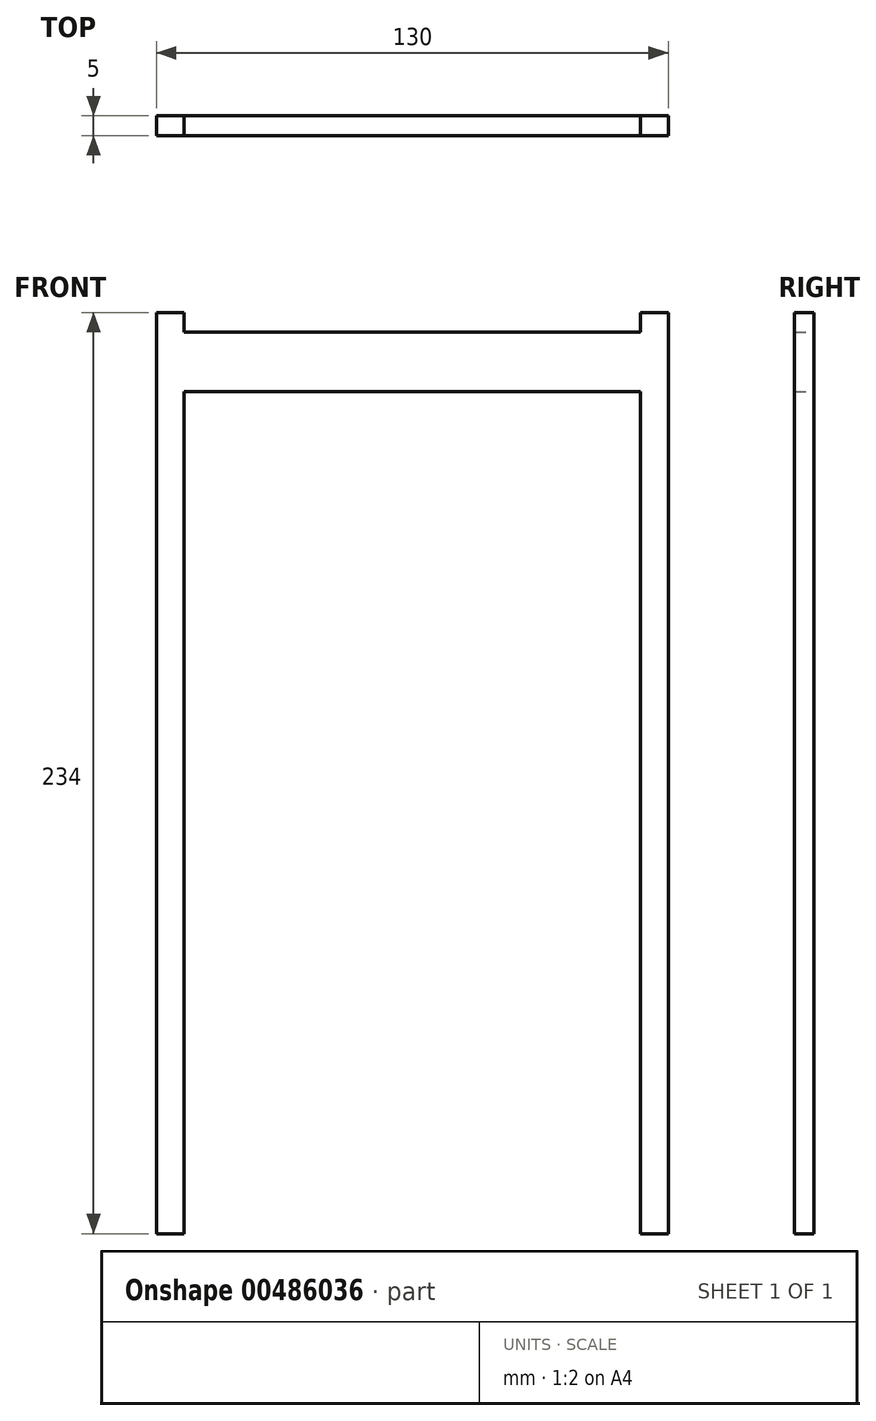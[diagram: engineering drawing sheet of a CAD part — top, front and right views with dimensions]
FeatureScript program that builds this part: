
annotation { "Feature Type Name" : "Feature", "Feature Type Description" : "" }
export const myFeature = defineFeature(function(context is Context, id is Id, definition is map)
    precondition{}
    {
        {
            var Q0;
            Q0=qCreatedBy(makeId("Front.planeOp"),FACE);
            var sketch = newSketch(context, id + "F0", { "sketchPlane" : qUnion([Q0])});
            skLineSegment(sketch, "E0.bottom", {"start": v(-65, -115.52) * mm, "end": v(-58, -115.52) * mm});
            skLineSegment(sketch, "E0.top", {"start": v(-65, 118.48) * mm, "end": v(-58, 118.48) * mm});
            skLineSegment(sketch, "E0.left", {"start": v(-65, -115.52) * mm, "end": v(-65, 118.48) * mm});
            skLineSegment(sketch, "E0.right", {"start": v(-58, -115.52) * mm, "end": v(-58, 118.48) * mm});
            skLineSegment(sketch, "E1.bottom", {"start": v(-58, 113.48) * mm, "end": v(0, 113.48) * mm});
            skLineSegment(sketch, "E1.top", {"start": v(-58, 98.48) * mm, "end": v(0, 98.48) * mm});
            skLineSegment(sketch, "E1.left", {"start": v(-58, 113.48) * mm, "end": v(-58, 98.48) * mm});
            skLineSegment(sketch, "E1.right", {"start": v(0, 113.48) * mm, "end": v(0, 98.48) * mm});
            skLineSegment(sketch, "E2.MirrorCS", {"start": v(65, 118.48) * mm, "end": v(58, 118.48) * mm});
            skLineSegment(sketch, "E3.MirrorCS", {"start": v(65, -115.52) * mm, "end": v(58, -115.52) * mm});
            skLineSegment(sketch, "E4.MirrorCS", {"start": v(58, 113.48) * mm, "end": v(58, 98.48) * mm});
            skLineSegment(sketch, "E5.MirrorCS", {"start": v(58, 98.48) * mm, "end": v(0, 98.48) * mm});
            skLineSegment(sketch, "E6.MirrorCS", {"start": v(58, 113.48) * mm, "end": v(0, 113.48) * mm});
            skLineSegment(sketch, "E7.MirrorCS", {"start": v(58, -115.52) * mm, "end": v(58, 118.48) * mm});
            skLineSegment(sketch, "E8.MirrorCS", {"start": v(65, -115.52) * mm, "end": v(65, 118.48) * mm});
            skSolve(sketch);
        }
        {
            var Q0;
            Q0=makeQuery(id+"F0.imprint","IMPRINT",FACE,{"disambiguationData":[TD([[makeQuery(id+"F0.imprint","IMPRINT",EDGE,{"derivedFrom":sQuery(id+"F0.wireOp",EDGE,"E1.bottom")}),-1.0]])]});
            var Q1;
            {var subQ1=sQuery(id+"F0.wireOp",EDGE,"E0.bottom");Q1=makeQuery(id+"F0.imprint","IMPRINT",FACE,{"disambiguationData":[TD([[makeQuery(id+"F0.imprint","IMPRINT",EDGE,{"derivedFrom":subQ1}),1.0]])]});}
            var Q2;
            Q2=makeQuery(id+"F0.imprint","IMPRINT",FACE,{"disambiguationData":[TD([[makeQuery(id+"F0.imprint","IMPRINT",EDGE,{"derivedFrom":sQuery(id+"F0.wireOp",EDGE,"E1.right")}),1.0]])]});
            var Q3;
            {var subQ4=sQuery(id+"F0.wireOp",EDGE,"E2.MirrorCS");Q3=makeQuery(id+"F0.imprint","IMPRINT",FACE,{"disambiguationData":[TD([[makeQuery(id+"F0.imprint","IMPRINT",EDGE,{"derivedFrom":subQ4}),1.0]])]});}
            extrude(context, id + "F1", {"entities" : qUnion([Q0, Q1, Q2, Q3]), "depth" : 5 * mm});
        }
    });
